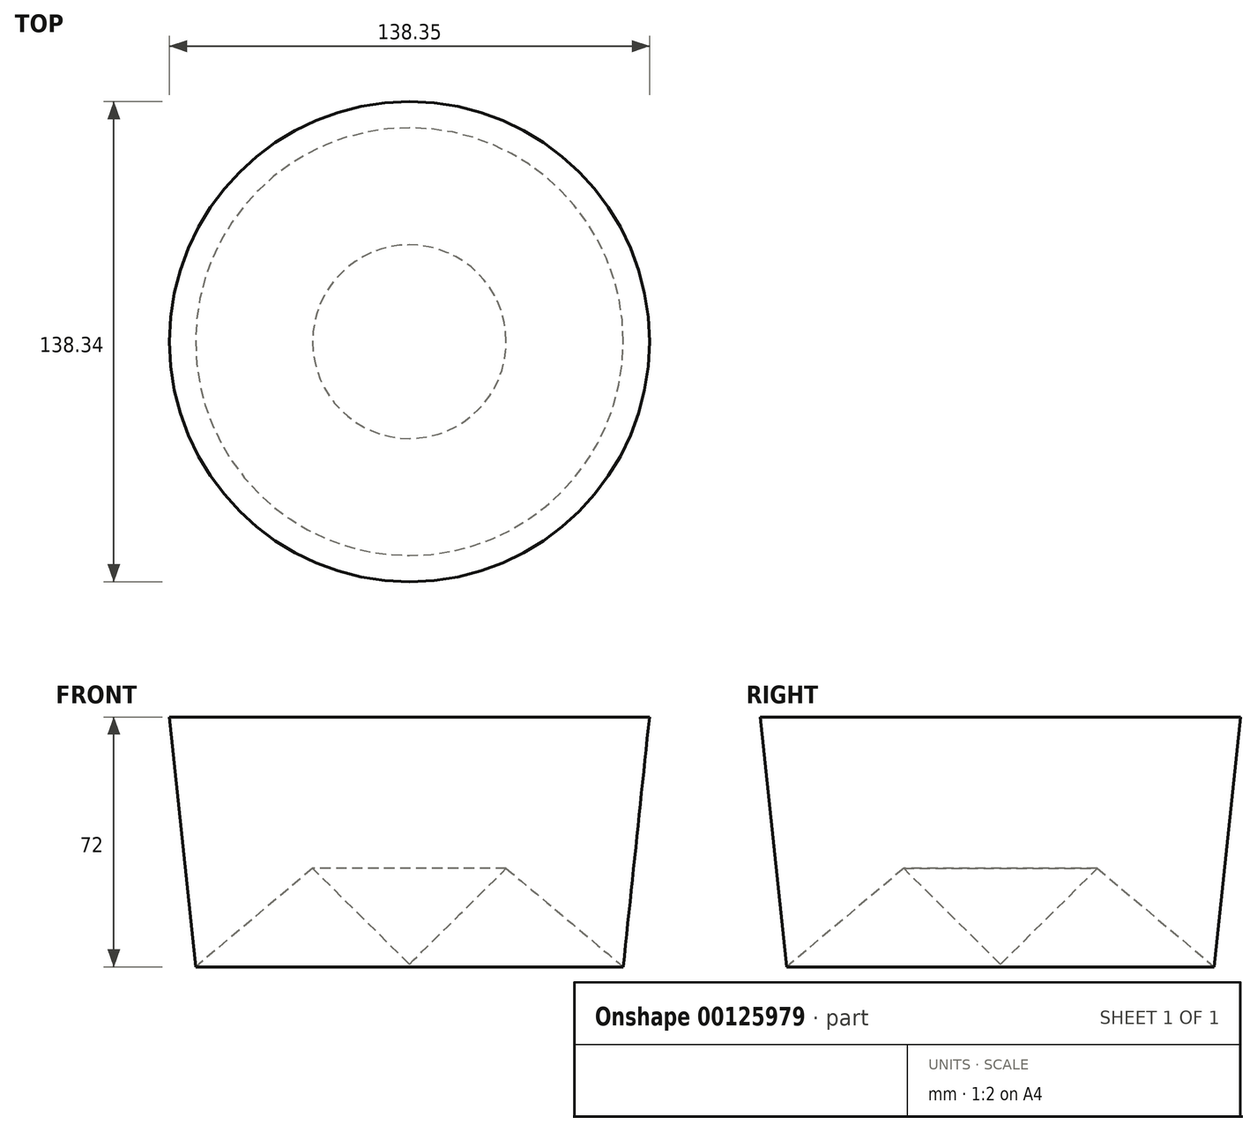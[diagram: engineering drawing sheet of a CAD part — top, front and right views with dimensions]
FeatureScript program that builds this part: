
annotation { "Feature Type Name" : "Feature", "Feature Type Description" : "" }
export const myFeature = defineFeature(function(context is Context, id is Id, definition is map)
    precondition{}
    {
        {
            var Q0;
            Q0=qCreatedBy(makeId("Front.planeOp"),FACE);
            var sketch = newSketch(context, id + "F0", { "sketchPlane" : qUnion([Q0])});
            skLineSegment(sketch, "E0", {"start": v(-88.59, 43.63) * mm, "end": v(-19.41, 43.63) * mm});
            skLineSegment(sketch, "E1", {"start": v(-19.41, 43.63) * mm, "end": v(-19.41, -27.61) * mm});
            skLineSegment(sketch, "E2", {"start": v(-19.41, -27.61) * mm, "end": v(-47.3, 0) * mm});
            skLineSegment(sketch, "E3", {"start": v(-47.3, 0) * mm, "end": v(-81.05, -28.37) * mm});
            skLineSegment(sketch, "E4", {"start": v(-81.05, -28.37) * mm, "end": v(-88.59, 43.63) * mm});
            skSolve(sketch);
        }
        {
            var Q0;
            Q0=makeQuery(id+"F0.imprint","IMPRINT",FACE,{"disambiguationData":[TD([[makeQuery(id+"F0.imprint","IMPRINT",EDGE,{"derivedFrom":sQuery(id+"F0.wireOp",EDGE,"E0")}),-1.0]])]});
            var Q1;
            Q1=sQuery(id+"F0.wireOp",EDGE,"E1");
            revolve(context, id + "F1", {"entities" : qUnion([Q0]), "axis" : qUnion([Q1]), "revolveType" : RevolveType.FULL});
        }
    });
